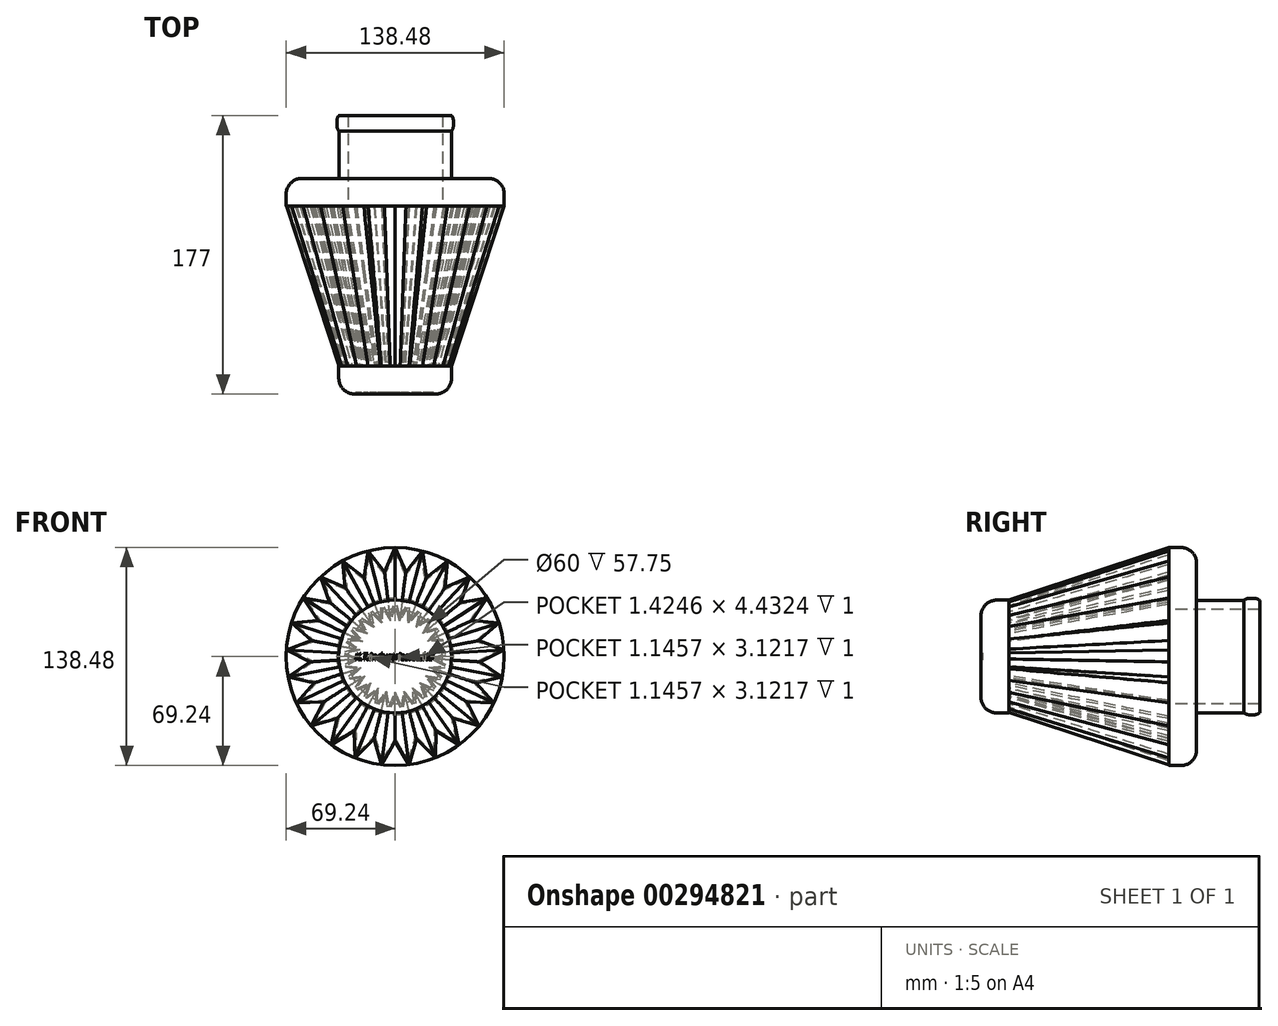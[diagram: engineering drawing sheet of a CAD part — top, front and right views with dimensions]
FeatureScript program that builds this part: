
annotation { "Feature Type Name" : "Feature", "Feature Type Description" : "" }
export const myFeature = defineFeature(function(context is Context, id is Id, definition is map)
    precondition{}
    {
        {
            var Q0;
            Q0=qCreatedBy(makeId("Front.planeOp"),FACE);
            var sketch = newSketch(context, id + "F0", { "sketchPlane" : qUnion([Q0])});
            skLineSegment(sketch, "E0", {"start": v(0, 0) * mm, "end": v(0, 69.24) * mm, "construction": true});
            skLineSegment(sketch, "E1", {"start": v(0, 69.24) * mm, "end": v(-8.68, 49.24) * mm});
            skLineSegment(sketch, "E2", {"start": v(-8.68, 49.24) * mm, "end": v(0, 0) * mm});
            skLineSegment(sketch, "E3.MirrorCS", {"start": v(0, 69.24) * mm, "end": v(8.68, 49.24) * mm});
            skLineSegment(sketch, "E4.MirrorCS", {"start": v(8.68, 49.24) * mm, "end": v(0, 0) * mm});
            skSolve(sketch);
        }
        {
            var Q0;
            Q0=qCreatedBy(makeId("Front.planeOp"),FACE);
            cPlane(context, id + "F1", {"entities" : qUnion([Q0]), "cplaneType" : CPlaneType.OFFSET, "offset" : 101.5 * mm, "width" : 150 * mm, "height" : 150 * mm});
        }
        {
            var Q0;
            Q0=qCreatedBy(id+"F1.planeOp",FACE);
            var sketch = newSketch(context, id + "F2", { "sketchPlane" : qUnion([Q0])});
            skLineSegment(sketch, "E5.0", {"start": v(0, 0) * mm, "end": v(0, 69.24) * mm, "construction": true});
            skLineSegment(sketch, "E6", {"start": v(0, 0) * mm, "end": v(-3.26, 24.79) * mm});
            skLineSegment(sketch, "E7", {"start": v(-3.26, 24.79) * mm, "end": v(0, 35.81) * mm});
            skLineSegment(sketch, "E8.MirrorCS", {"start": v(3.26, 24.79) * mm, "end": v(0, 35.81) * mm});
            skLineSegment(sketch, "E9.MirrorCS", {"start": v(0, 0) * mm, "end": v(3.26, 24.79) * mm});
            skSolve(sketch);
        }
        {
            var Q0;
            Q0=makeQuery(id+"F0.imprint","IMPRINT",FACE,{"disambiguationData":[TD([[makeQuery(id+"F0.imprint","IMPRINT",EDGE,{"derivedFrom":sQuery(id+"F0.wireOp",EDGE,"E1")}),1.0]])]});
            var Q1;
            Q1=makeQuery(id+"F2.imprint","IMPRINT",FACE,{"disambiguationData":[TD([[makeQuery(id+"F2.imprint","IMPRINT",EDGE,{"derivedFrom":sQuery(id+"F2.wireOp",EDGE,"E6")}),-1.0]])]});
            loft(context, id + "F3", {"sheetProfilesArray" : [{ "sheetProfileEntities" : qUnion([Q0]) }, { "sheetProfileEntities" : qUnion([Q1]) }]});
        }
        {
            var Q0;
            Q0=qCreatedBy(makeId("Right.planeOp"),FACE);
            var sketch = newSketch(context, id + "F4", { "sketchPlane" : qUnion([Q0])});
            skLineSegment(sketch, "E10", {"start": v(0, 0) * mm, "end": v(-101.5, 0) * mm, "construction": true});
            skSolve(sketch);
        }
        {
            var Q0;
            Q0=makeQuery(id+"F3.opLoft","SWEPT_BODY",BODY,{"disambiguationData":[OSD([makeQuery(id+"F0.imprint","IMPRINT",FACE,{"disambiguationData":[TD([[makeQuery(id+"F0.imprint","IMPRINT",EDGE,{"derivedFrom":sQuery(id+"F0.wireOp",EDGE,"E1")}),1.0]])]}),makeQuery(id+"F2.imprint","IMPRINT",FACE,{"disambiguationData":[TD([[makeQuery(id+"F2.imprint","IMPRINT",EDGE,{"derivedFrom":sQuery(id+"F2.wireOp",EDGE,"E6")}),-1.0]])]})])]});
            var Q1;
            Q1=makeQuery(id+"F3.opLoft","SWEPT_FACE",FACE,{"disambiguationData":[OSD([sQuery(id+"F0.wireOp",EDGE,"E2"),sQuery(id+"F0.wireOp",EDGE,"E3.MirrorCS"),sQuery(id+"F0.wireOp",EDGE,"E4.MirrorCS"),sQuery(id+"F2.wireOp",EDGE,"E6"),sQuery(id+"F2.wireOp",EDGE,"E8.MirrorCS"),sQuery(id+"F2.wireOp",EDGE,"E9.MirrorCS")])]});
            var Q2;
            Q2=sQuery(id+"F4.wireOp",EDGE,"E10");
            circularPattern(context, id + "F5", {"operationType" : NewBodyOperationType.ADD, "entities" : qUnion([Q0]), "axis" : qUnion([Q2]), "angle" : 360 * degree, "instanceCount" : round(25), "oppositeDirection" : true, "equalSpace" : true});
        }
        {
            var Q0;
            {var subQ0=makeQuery(id+"F3.opLoft","CAP_FACE",FACE,{"disambiguationData":[OSD([makeQuery(id+"F2.imprint","IMPRINT",FACE,{"disambiguationData":[TD([[makeQuery(id+"F2.imprint","IMPRINT",EDGE,{"derivedFrom":sQuery(id+"F2.wireOp",EDGE,"E6")}),-1.0]])]})])],"isStart":true});Q0=makeQuery(id+"F5.boolean.opBoolean","MERGE",FACE,{"derivedFrom":[subQ0,makeQuery(id+"F5.opPattern","COPY",FACE,{"derivedFrom":subQ0,"instanceName":"1"}),makeQuery(id+"F5.opPattern","COPY",FACE,{"derivedFrom":subQ0,"instanceName":"2"}),makeQuery(id+"F5.opPattern","COPY",FACE,{"derivedFrom":subQ0,"instanceName":"3"}),makeQuery(id+"F5.opPattern","COPY",FACE,{"derivedFrom":subQ0,"instanceName":"4"}),makeQuery(id+"F5.opPattern","COPY",FACE,{"derivedFrom":subQ0,"instanceName":"5"}),makeQuery(id+"F5.opPattern","COPY",FACE,{"derivedFrom":subQ0,"instanceName":"6"}),makeQuery(id+"F5.opPattern","COPY",FACE,{"derivedFrom":subQ0,"instanceName":"7"}),makeQuery(id+"F5.opPattern","COPY",FACE,{"derivedFrom":subQ0,"instanceName":"8"}),makeQuery(id+"F5.opPattern","COPY",FACE,{"derivedFrom":subQ0,"instanceName":"9"}),makeQuery(id+"F5.opPattern","COPY",FACE,{"derivedFrom":subQ0,"instanceName":"10"}),makeQuery(id+"F5.opPattern","COPY",FACE,{"derivedFrom":subQ0,"instanceName":"11"}),makeQuery(id+"F5.opPattern","COPY",FACE,{"derivedFrom":subQ0,"instanceName":"12"}),makeQuery(id+"F5.opPattern","COPY",FACE,{"derivedFrom":subQ0,"instanceName":"13"}),makeQuery(id+"F5.opPattern","COPY",FACE,{"derivedFrom":subQ0,"instanceName":"14"}),makeQuery(id+"F5.opPattern","COPY",FACE,{"derivedFrom":subQ0,"instanceName":"15"}),makeQuery(id+"F5.opPattern","COPY",FACE,{"derivedFrom":subQ0,"instanceName":"16"}),makeQuery(id+"F5.opPattern","COPY",FACE,{"derivedFrom":subQ0,"instanceName":"17"}),makeQuery(id+"F5.opPattern","COPY",FACE,{"derivedFrom":subQ0,"instanceName":"18"}),makeQuery(id+"F5.opPattern","COPY",FACE,{"derivedFrom":subQ0,"instanceName":"19"}),makeQuery(id+"F5.opPattern","COPY",FACE,{"derivedFrom":subQ0,"instanceName":"20"}),makeQuery(id+"F5.opPattern","COPY",FACE,{"derivedFrom":subQ0,"instanceName":"21"}),makeQuery(id+"F5.opPattern","COPY",FACE,{"derivedFrom":subQ0,"instanceName":"22"}),makeQuery(id+"F5.opPattern","COPY",FACE,{"derivedFrom":subQ0,"instanceName":"23"}),makeQuery(id+"F5.opPattern","COPY",FACE,{"derivedFrom":subQ0,"instanceName":"24"})]});}
            var Q1;
            {var subQ0=makeQuery(id+"F3.opLoft","CAP_FACE",FACE,{"disambiguationData":[OSD([makeQuery(id+"F0.imprint","IMPRINT",FACE,{"disambiguationData":[TD([[makeQuery(id+"F0.imprint","IMPRINT",EDGE,{"derivedFrom":sQuery(id+"F0.wireOp",EDGE,"E1")}),1.0]])]})])],"isStart":true});Q1=makeQuery(id+"F5.boolean.opBoolean","MERGE",FACE,{"derivedFrom":[subQ0,makeQuery(id+"F5.opPattern","COPY",FACE,{"derivedFrom":subQ0,"instanceName":"1"}),makeQuery(id+"F5.opPattern","COPY",FACE,{"derivedFrom":subQ0,"instanceName":"2"}),makeQuery(id+"F5.opPattern","COPY",FACE,{"derivedFrom":subQ0,"instanceName":"3"}),makeQuery(id+"F5.opPattern","COPY",FACE,{"derivedFrom":subQ0,"instanceName":"4"}),makeQuery(id+"F5.opPattern","COPY",FACE,{"derivedFrom":subQ0,"instanceName":"5"}),makeQuery(id+"F5.opPattern","COPY",FACE,{"derivedFrom":subQ0,"instanceName":"6"}),makeQuery(id+"F5.opPattern","COPY",FACE,{"derivedFrom":subQ0,"instanceName":"7"}),makeQuery(id+"F5.opPattern","COPY",FACE,{"derivedFrom":subQ0,"instanceName":"8"}),makeQuery(id+"F5.opPattern","COPY",FACE,{"derivedFrom":subQ0,"instanceName":"9"}),makeQuery(id+"F5.opPattern","COPY",FACE,{"derivedFrom":subQ0,"instanceName":"10"}),makeQuery(id+"F5.opPattern","COPY",FACE,{"derivedFrom":subQ0,"instanceName":"11"}),makeQuery(id+"F5.opPattern","COPY",FACE,{"derivedFrom":subQ0,"instanceName":"12"}),makeQuery(id+"F5.opPattern","COPY",FACE,{"derivedFrom":subQ0,"instanceName":"13"}),makeQuery(id+"F5.opPattern","COPY",FACE,{"derivedFrom":subQ0,"instanceName":"14"}),makeQuery(id+"F5.opPattern","COPY",FACE,{"derivedFrom":subQ0,"instanceName":"15"}),makeQuery(id+"F5.opPattern","COPY",FACE,{"derivedFrom":subQ0,"instanceName":"16"}),makeQuery(id+"F5.opPattern","COPY",FACE,{"derivedFrom":subQ0,"instanceName":"17"}),makeQuery(id+"F5.opPattern","COPY",FACE,{"derivedFrom":subQ0,"instanceName":"18"}),makeQuery(id+"F5.opPattern","COPY",FACE,{"derivedFrom":subQ0,"instanceName":"19"}),makeQuery(id+"F5.opPattern","COPY",FACE,{"derivedFrom":subQ0,"instanceName":"20"}),makeQuery(id+"F5.opPattern","COPY",FACE,{"derivedFrom":subQ0,"instanceName":"21"}),makeQuery(id+"F5.opPattern","COPY",FACE,{"derivedFrom":subQ0,"instanceName":"22"}),makeQuery(id+"F5.opPattern","COPY",FACE,{"derivedFrom":subQ0,"instanceName":"23"}),makeQuery(id+"F5.opPattern","COPY",FACE,{"derivedFrom":subQ0,"instanceName":"24"})]});}
            shell(context, id + "F6", {"entities" : qUnion([Q0, Q1]), "thickness" : 1 * mm});
        }
        {
            var Q0;
            Q0=qCreatedBy(makeId("Front.planeOp"),FACE);
            var sketch = newSketch(context, id + "F7", { "sketchPlane" : qUnion([Q0])});
            skCircle(sketch, "E11", {"center": v(0, 0) * mm, "radius": 69.24 * mm});
            skCircle(sketch, "E12", {"center": v(0, 0) * mm, "radius": 30 * mm});
            skSolve(sketch);
        }
        {
            var Q0;
            Q0=qSketchRegion(id+"F7",true);
            extrude(context, id + "F8", {"entities" : qUnion([Q0]), "oppositeDirection" : true, "depth" : 17.75 * mm});
        }
        {
            var Q0;
            Q0=qCreatedBy(id+"F1.planeOp",FACE);
            var sketch = newSketch(context, id + "F9", { "sketchPlane" : qUnion([Q0])});
            skCircle(sketch, "E13", {"center": v(0, 0) * mm, "radius": 35.81 * mm});
            skSolve(sketch);
        }
        {
            var Q0;
            Q0=makeQuery(id+"F9.imprint","IMPRINT",FACE,{"disambiguationData":[TD([[makeQuery(id+"F9.imprint","IMPRINT",EDGE,{"derivedFrom":sQuery(id+"F9.wireOp",EDGE,"E13")}),1.0]])]});
            extrude(context, id + "F10", {"entities" : qUnion([Q0]), "depth" : 17.75 * mm});
        }
        {
            var Q0;
            Q0=makeQuery(id+"F8.opExtrude","CAP_FACE",FACE,{"disambiguationData":[OSD([sQuery(id+"F7.wireOp",EDGE,"E11"),sQuery(id+"F7.wireOp",EDGE,"E12")])],"isStart":false});
            var sketch = newSketch(context, id + "F11", { "sketchPlane" : qUnion([Q0])});
            skCircle(sketch, "E14", {"center": v(0, 0) * mm, "radius": 35.76 * mm});
            skSolve(sketch);
        }
        {
            var Q0;
            Q0=makeQuery(id+"F11.imprint","IMPRINT",FACE,{"disambiguationData":[TD([[makeQuery(id+"F11.imprint","IMPRINT",EDGE,{"derivedFrom":sQuery(id+"F11.wireOp",EDGE,"E14")}),1.0]])]});
            extrude(context, id + "F12", {"entities" : qUnion([Q0]), "operationType" : NewBodyOperationType.ADD, "depth" : 35 * mm});
        }
        {
            var Q0;
            Q0=makeQuery(id+"F12.opExtrude","CAP_FACE",FACE,{"disambiguationData":[OSD([sQuery(id+"F7.wireOp",EDGE,"E12"),sQuery(id+"F11.wireOp",EDGE,"E14")])],"isStart":false});
            var sketch = newSketch(context, id + "F13", { "sketchPlane" : qUnion([Q0])});
            skCircle(sketch, "E15", {"center": v(0, 0) * mm, "radius": 37 * mm});
            skSolve(sketch);
        }
        {
            var Q0;
            Q0=makeQuery(id+"F13.imprint","IMPRINT",FACE,{"disambiguationData":[TD([[makeQuery(id+"F13.imprint","IMPRINT",EDGE,{"derivedFrom":sQuery(id+"F13.wireOp",EDGE,"E15")}),1.0]])]});
            extrude(context, id + "F14", {"entities" : qUnion([Q0]), "operationType" : NewBodyOperationType.ADD, "endBound" : BoundingType.SYMMETRIC, "depth" : 10 * mm});
        }
        {
            var Q0;
            Q0=makeQuery(id+"F10.opExtrude","CAP_FACE",FACE,{"disambiguationData":[OSD([sQuery(id+"F9.wireOp",EDGE,"E13")])],"isStart":false});
            var sketch = newSketch(context, id + "F15", { "sketchPlane" : qUnion([Q0])});
            skText(sketch, "E16", { "text": "K.T.industries.co.ltd", "fontName": "OpenSans-Italic.ttf"});
            const initialGuessF15  = {"E16": [-0.02549, -0.00219, 1, 0, 0.0042]};
            skSetInitialGuess(sketch, initialGuessF15);
            skSolve(sketch);
        }
        {
            var Q0;
            Q0=qSketchRegion(id+"F15",true);
            extrude(context, id + "F16", {"entities" : qUnion([Q0]), "operationType" : NewBodyOperationType.REMOVE, "oppositeDirection" : true, "depth" : 1 * mm});
        }
        {
            var Q0;
            Q0=makeQuery(id+"F10.opExtrude","CAP_EDGE",EDGE,{"disambiguationData":[OSD([sQuery(id+"F9.wireOp",EDGE,"E13")])],"isStart":false});
            var Q1;
            Q1=makeQuery(id+"F8.opExtrude","CAP_EDGE",EDGE,{"disambiguationData":[OSD([sQuery(id+"F7.wireOp",EDGE,"E11")])],"isStart":false});
            fillet(context, id + "F17", {"entities" : qUnion([Q0, Q1]), "radius" : 10 * mm, "tangentPropagation" : true, "allowEdgeOverflow" : false});
        }
        {
            var Q0;
            Q0=makeQuery(id+"F14.opExtrude","CAP_EDGE",EDGE,{"disambiguationData":[OSD([sQuery(id+"F13.wireOp",EDGE,"E15")])],"isStart":false});
            var Q1;
            Q1=makeQuery(id+"F14.opExtrude","CAP_EDGE",EDGE,{"disambiguationData":[OSD([sQuery(id+"F13.wireOp",EDGE,"E15")])],"isStart":true});
            fillet(context, id + "F18", {"entities" : qUnion([Q0, Q1]), "radius" : 6 * mm, "tangentPropagation" : true, "allowEdgeOverflow" : false});
        }
        {
            var Q0;
            Q0=makeQuery(id+"F12.opExtrude","CAP_FACE",FACE,{"disambiguationData":[OSD([sQuery(id+"F7.wireOp",EDGE,"E12"),sQuery(id+"F11.wireOp",EDGE,"E14")])],"isStart":false});
            extrude(context, id + "F19", {"entities" : qUnion([Q0]), "operationType" : NewBodyOperationType.ADD, "depth" : 5 * mm});
        }
    });
